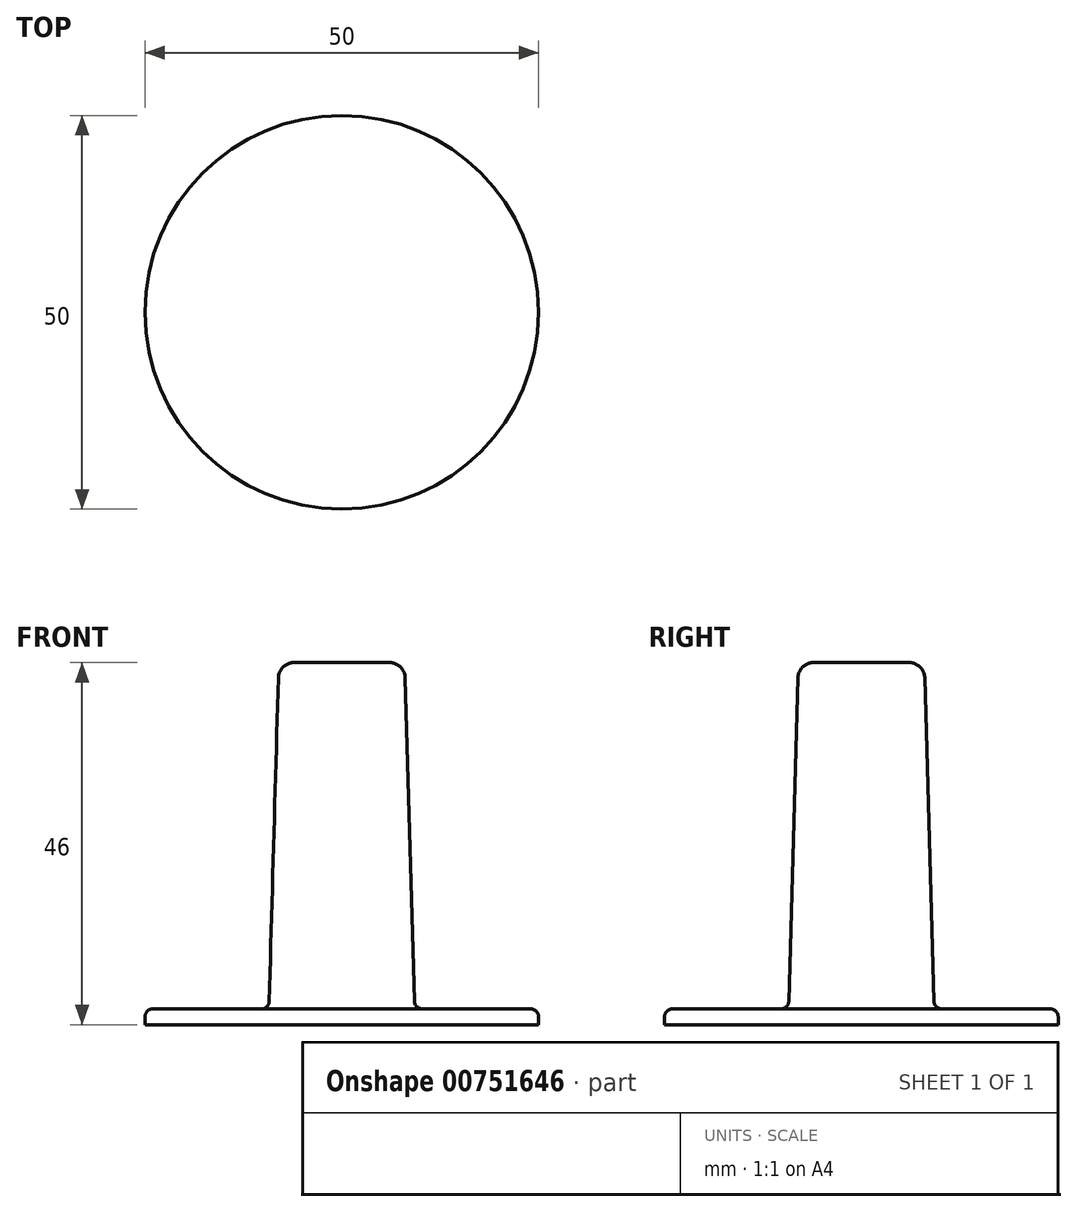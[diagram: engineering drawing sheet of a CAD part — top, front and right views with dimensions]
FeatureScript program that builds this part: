
annotation { "Feature Type Name" : "Feature", "Feature Type Description" : "" }
export const myFeature = defineFeature(function(context is Context, id is Id, definition is map)
    precondition{}
    {
        {
            var Q0;
            Q0=qCreatedBy(makeId("Front.planeOp"),FACE);
            var sketch = newSketch(context, id + "F0", { "sketchPlane" : qUnion([Q0])});
            skLineSegment(sketch, "E0", {"start": v(0, 0) * mm, "end": v(-25, 0) * mm});
            skLineSegment(sketch, "E1", {"start": v(-25, 0) * mm, "end": v(-25, 2) * mm});
            skLineSegment(sketch, "E2", {"start": v(-25, 2) * mm, "end": v(-9.25, 2) * mm});
            skLineSegment(sketch, "E3", {"start": v(-9.25, 2) * mm, "end": v(-8, 46) * mm});
            skLineSegment(sketch, "E4", {"start": v(-8, 46) * mm, "end": v(0, 46) * mm});
            skLineSegment(sketch, "E5", {"start": v(0, 46) * mm, "end": v(0, 0) * mm});
            skLineSegment(sketch, "E6.MirrorCS", {"start": v(25, 0) * mm, "end": v(25, 2) * mm});
            skLineSegment(sketch, "E7.MirrorCS", {"start": v(0, 0) * mm, "end": v(25, 0) * mm});
            skLineSegment(sketch, "E8.MirrorCS", {"start": v(25, 2) * mm, "end": v(9.25, 2) * mm});
            skLineSegment(sketch, "E9.MirrorCS", {"start": v(8, 46) * mm, "end": v(0, 46) * mm});
            skLineSegment(sketch, "E10.MirrorCS", {"start": v(9.25, 2) * mm, "end": v(8, 46) * mm});
            skSolve(sketch);
        }
        {
            var Q0;
            Q0=makeQuery(id+"F0.imprint","IMPRINT",FACE,{"disambiguationData":[TD([[makeQuery(id+"F0.imprint","IMPRINT",EDGE,{"derivedFrom":sQuery(id+"F0.wireOp",EDGE,"E0")}),-1.0]])]});
            var Q1;
            Q1=sQuery(id+"F0.wireOp",EDGE,"E5");
            revolve(context, id + "F1", {"surfaceOperationType" : NewSurfaceOperationType.NEW, "entities" : qUnion([Q0]), "axis" : qUnion([Q1]), "revolveType" : RevolveType.FULL});
        }
        {
            var Q0;
            Q0=makeQuery(id+"F1.opRevolve","SWEPT_EDGE",EDGE,{"disambiguationData":[OSD([sQuery(id+"F0.wireOp",EDGE,"E3"),sQuery(id+"F0.wireOp",EDGE,"E4")])]});
            fillet(context, id + "F2", {"entities" : qUnion([Q0]), "radius" : 2 * mm, "tangentPropagation" : true, "allowEdgeOverflow" : false});
        }
        {
            var Q0;
            Q0=makeQuery(id+"F1.opRevolve","SWEPT_EDGE",EDGE,{"disambiguationData":[OSD([sQuery(id+"F0.wireOp",EDGE,"E1"),sQuery(id+"F0.wireOp",EDGE,"E2")])]});
            fillet(context, id + "F3", {"entities" : qUnion([Q0]), "radius" : 1 * mm, "tangentPropagation" : true, "allowEdgeOverflow" : false});
        }
        {
            var Q0;
            Q0=makeQuery(id+"F1.opRevolve","SWEPT_EDGE",EDGE,{"disambiguationData":[OSD([sQuery(id+"F0.wireOp",EDGE,"E2"),sQuery(id+"F0.wireOp",EDGE,"E3")])]});
            fillet(context, id + "F4", {"entities" : qUnion([Q0]), "radius" : 1 * mm, "tangentPropagation" : true, "allowEdgeOverflow" : false});
        }
    });
